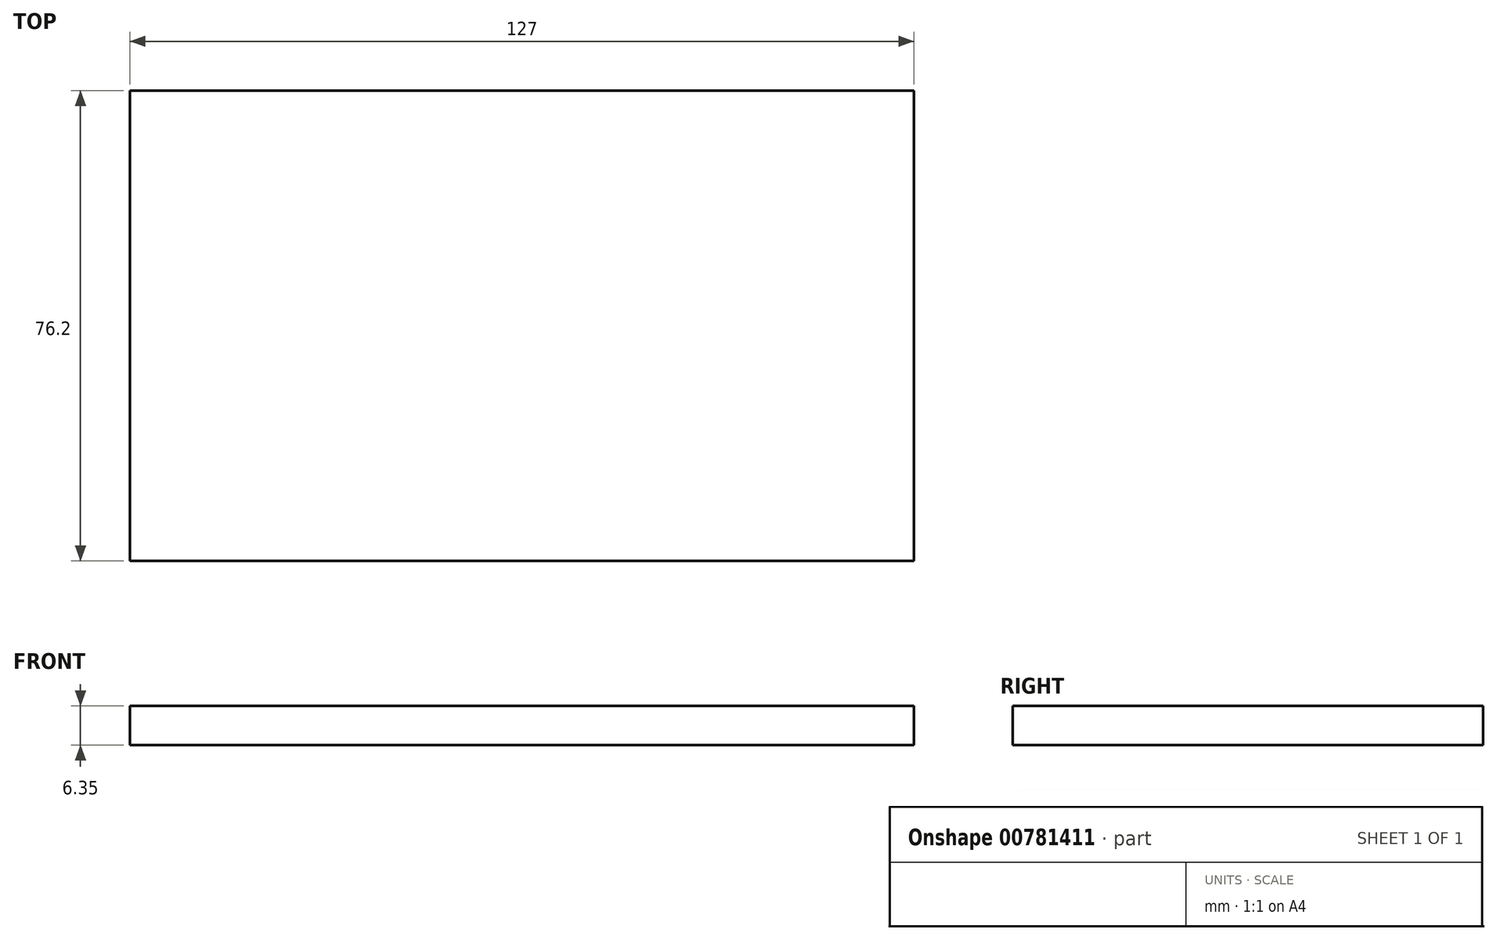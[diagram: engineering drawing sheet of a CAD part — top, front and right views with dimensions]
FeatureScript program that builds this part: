
annotation { "Feature Type Name" : "Feature", "Feature Type Description" : "" }
export const myFeature = defineFeature(function(context is Context, id is Id, definition is map)
    precondition{}
    {
        {
            var Q0;
            Q0=qCreatedBy(makeId("Top.planeOp"),FACE);
            var sketch = newSketch(context, id + "F0", { "sketchPlane" : qUnion([Q0])});
            skLineSegment(sketch, "E0.bottom", {"start": v(63.5, -38.1) * mm, "end": v(-63.5, -38.1) * mm});
            skLineSegment(sketch, "E0.top", {"start": v(63.5, 38.1) * mm, "end": v(-63.5, 38.1) * mm});
            skLineSegment(sketch, "E0.left", {"start": v(63.5, -38.1) * mm, "end": v(63.5, 38.1) * mm});
            skLineSegment(sketch, "E0.right", {"start": v(-63.5, -38.1) * mm, "end": v(-63.5, 38.1) * mm});
            skPoint(sketch, "E0.middle", {"position": v(0, 0) * mm});
            skSolve(sketch);
        }
        {
            var Q0;
            Q0=makeQuery(id+"F0.imprint","IMPRINT",FACE,{"disambiguationData":[TD([[makeQuery(id+"F0.imprint","IMPRINT",EDGE,{"derivedFrom":sQuery(id+"F0.wireOp",EDGE,"E0.bottom")}),-1.0]])]});
            extrude(context, id + "F1", {"entities" : qUnion([Q0]), "depth" : 6.35 * mm, "offsetDistance" : 25.4 * mm});
        }
    });
